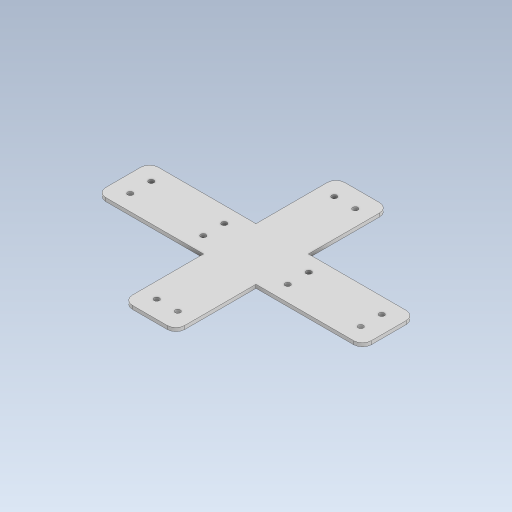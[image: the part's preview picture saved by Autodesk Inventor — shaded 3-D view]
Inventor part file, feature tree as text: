
AUTODESK INVENTOR PART (.ipt)
format: ipt  version: 2023.5 (Build 275446000, 446)  size: 137,216 bytes
history: native  units: in
note: dims shown in document units (in); Inventor stores cm internally (conversion verified against a paired STEP export)
features: extrude x1, sketch x1
ambient origin geometry x8: Origin, YZ Plane, XZ Plane, XY Plane, X Axis, Y Axis, Z Axis, Center Point
bodies: Solid1 (feature_tree)
feature tree (2):
  extrude  "Extrusion1"  Depth=0.0787in
  sketch  "Sketch1"  dims[d1=0.9498in d3=0.2362in d4=0.1181in d5=1.6437in d6=0.1181in d7=1.998in d8=0.2362in d9=0.5906in d10=0.3937in d11=0.5906in d12=0.3937in d13=0.1969in d14=0.1969in d15=0.0787in d16=0.0in]
